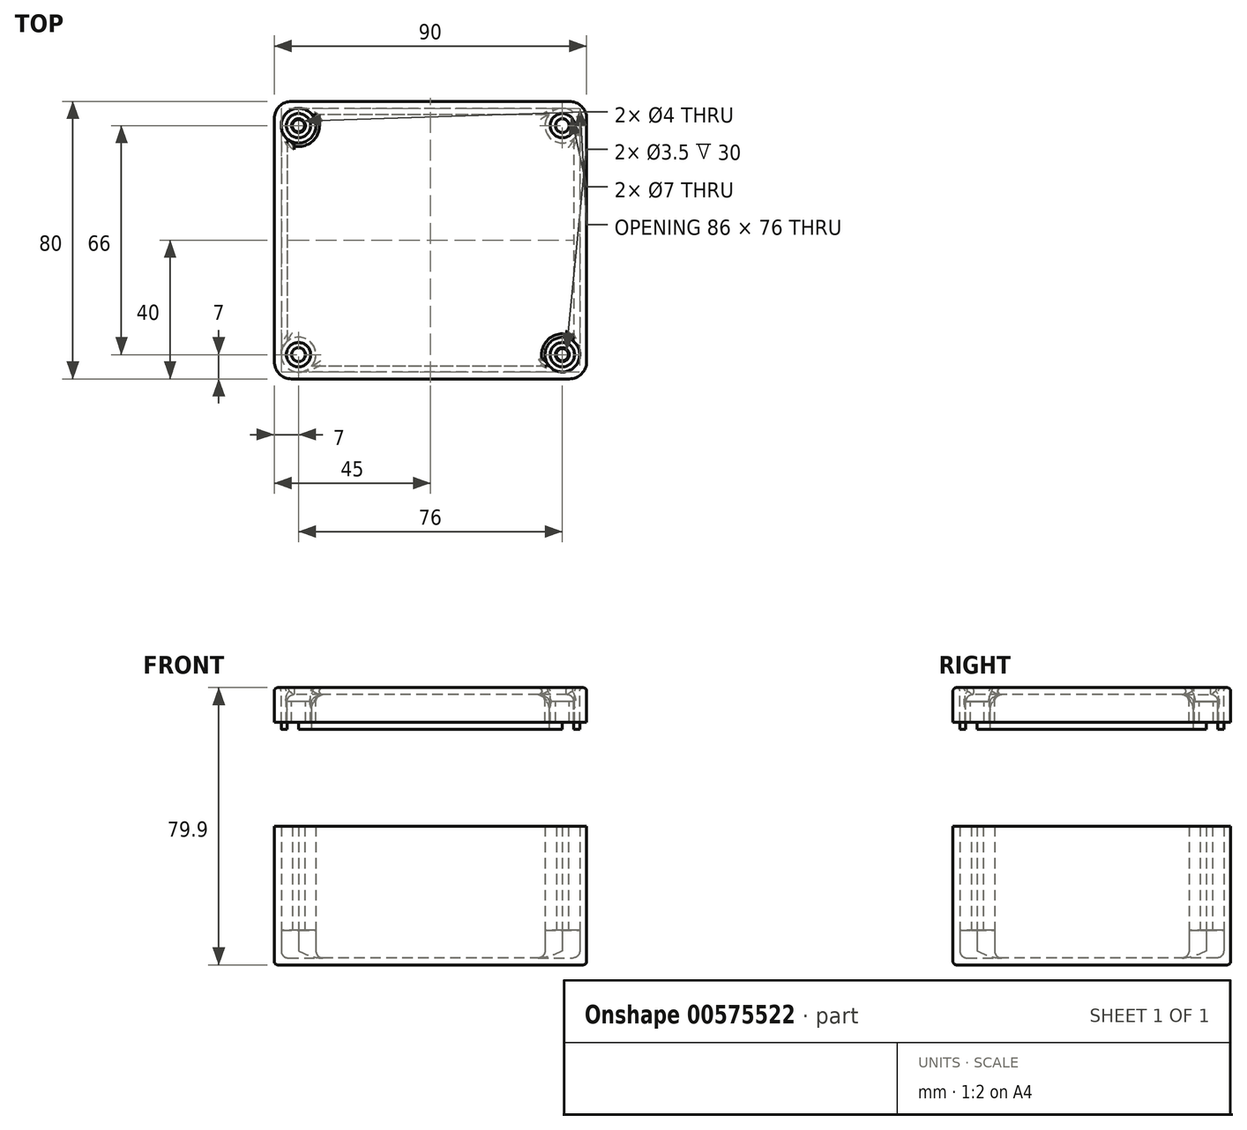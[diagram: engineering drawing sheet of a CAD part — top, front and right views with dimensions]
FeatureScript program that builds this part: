
annotation { "Feature Type Name" : "Feature", "Feature Type Description" : "" }
export const myFeature = defineFeature(function(context is Context, id is Id, definition is map)
    precondition{}
    {
        {
            var Q0;
            Q0=qCreatedBy(makeId("Top.planeOp"),FACE);
            var sketch = newSketch(context, id + "F0", { "sketchPlane" : qUnion([Q0])});
            skLineSegment(sketch, "E0.bottom", {"start": v(40, 40) * mm, "end": v(-40, 40) * mm});
            skLineSegment(sketch, "E0.top", {"start": v(40, -40) * mm, "end": v(-40, -40) * mm});
            skLineSegment(sketch, "E0.left", {"start": v(45, 35) * mm, "end": v(45, -35) * mm});
            skLineSegment(sketch, "E0.right", {"start": v(-45, 35) * mm, "end": v(-45, -35) * mm});
            skPoint(sketch, "E0.middle", {"position": v(0, 0) * mm});
            skPoint(sketch, "E1.visualSharp", {"position": v(-45, 40) * mm});
            skArc(sketch, "E1.filletArc", {"start": v(-40, 40) * mm, "mid": v(-43.54, 38.54) * mm, "end": v(-45, 35) * mm});
            skPoint(sketch, "E2.visualSharp", {"position": v(45, 40) * mm});
            skArc(sketch, "E2.filletArc", {"start": v(45, 35) * mm, "mid": v(43.54, 38.54) * mm, "end": v(40, 40) * mm});
            skPoint(sketch, "E3.visualSharp", {"position": v(-45, -40) * mm});
            skArc(sketch, "E3.filletArc", {"start": v(-45, -35) * mm, "mid": v(-43.54, -38.54) * mm, "end": v(-40, -40) * mm});
            skPoint(sketch, "E4.visualSharp", {"position": v(45, -40) * mm});
            skArc(sketch, "E4.filletArc", {"start": v(40, -40) * mm, "mid": v(43.54, -38.54) * mm, "end": v(45, -35) * mm});
            skLineSegment(sketch, "E5.0", {"start": v(38, -38) * mm, "end": v(-38, -38) * mm});
            skLineSegment(sketch, "E5.1", {"start": v(43, 33) * mm, "end": v(43, -33) * mm});
            skLineSegment(sketch, "E5.2", {"start": v(38, 38) * mm, "end": v(-38, 38) * mm});
            skLineSegment(sketch, "E5.3", {"start": v(-43, 33) * mm, "end": v(-43, -33) * mm});
            skPoint(sketch, "E6.visualSharp", {"position": v(43, 38) * mm});
            skArc(sketch, "E6.filletArc", {"start": v(43, 33) * mm, "mid": v(41.54, 36.54) * mm, "end": v(38, 38) * mm});
            skPoint(sketch, "E7.visualSharp", {"position": v(43, -38) * mm});
            skArc(sketch, "E7.filletArc", {"start": v(38, -38) * mm, "mid": v(41.54, -36.54) * mm, "end": v(43, -33) * mm});
            skPoint(sketch, "E8.visualSharp", {"position": v(-43, -38) * mm});
            skArc(sketch, "E8.filletArc", {"start": v(-43, -33) * mm, "mid": v(-41.54, -36.54) * mm, "end": v(-38, -38) * mm});
            skPoint(sketch, "E9.visualSharp", {"position": v(-43, 38) * mm});
            skArc(sketch, "E9.filletArc", {"start": v(-38, 38) * mm, "mid": v(-41.54, 36.54) * mm, "end": v(-43, 33) * mm});
            skLineSegment(sketch, "E10", {"start": v(0, 38) * mm, "end": v(0, -38) * mm, "construction": true});
            skCircle(sketch, "E11", {"center": v(-38, 33) * mm, "radius": 5 * mm});
            skCircle(sketch, "E12", {"center": v(-38, 33) * mm, "radius": 1.75 * mm});
            skLineSegment(sketch, "E13", {"start": v(-43, 0) * mm, "end": v(43, 0) * mm, "construction": true});
            skCircle(sketch, "E14.MirrorC", {"center": v(-38, -33) * mm, "radius": 5 * mm});
            skCircle(sketch, "E15.MirrorC", {"center": v(-38, -33) * mm, "radius": 1.75 * mm});
            skCircle(sketch, "E16.MirrorC", {"center": v(38, 33) * mm, "radius": 5 * mm});
            skCircle(sketch, "E17.MirrorC", {"center": v(38, 33) * mm, "radius": 1.75 * mm});
            skCircle(sketch, "E18.MirrorC", {"center": v(38, -33) * mm, "radius": 5 * mm});
            skCircle(sketch, "E19.MirrorC", {"center": v(38, -33) * mm, "radius": 1.75 * mm});
            skSolve(sketch);
        }
        {
            var Q0;
            {var subQ2=sQuery(id+"F0.wireOp",EDGE,"E5.0");Q0=makeQuery(id+"F0.imprint","IMPRINT",FACE,{"disambiguationData":[TD([[makeQuery(id+"F0.imprint","IMPRINT",EDGE,{"derivedFrom":subQ2}),-1.0]])]});}
            extrude(context, id + "F1", {"entities" : qUnion([Q0]), "depth" : 2 * mm, "offsetDistance" : 25 * mm});
        }
        {
            var Q0;
            Q0=makeQuery(id+"F0.imprint","IMPRINT",FACE,{"disambiguationData":[TD([[makeQuery(id+"F0.imprint","IMPRINT",EDGE,{"derivedFrom":sQuery(id+"F0.wireOp",EDGE,"E12")}),-1.0]])]});
            var Q1;
            Q1=makeQuery(id+"F0.imprint","IMPRINT",FACE,{"disambiguationData":[TD([[makeQuery(id+"F0.imprint","IMPRINT",EDGE,{"derivedFrom":sQuery(id+"F0.wireOp",EDGE,"E15.MirrorC")}),1.0]])]});
            var Q2;
            Q2=makeQuery(id+"F0.imprint","IMPRINT",FACE,{"disambiguationData":[TD([[makeQuery(id+"F0.imprint","IMPRINT",EDGE,{"derivedFrom":sQuery(id+"F0.wireOp",EDGE,"E0.bottom")}),1.0]])]});
            var Q3;
            Q3=makeQuery(id+"F0.imprint","IMPRINT",FACE,{"disambiguationData":[TD([[makeQuery(id+"F0.imprint","IMPRINT",EDGE,{"derivedFrom":sQuery(id+"F0.wireOp",EDGE,"E19.MirrorC")}),-1.0]])]});
            var Q4;
            Q4=makeQuery(id+"F0.imprint","IMPRINT",FACE,{"disambiguationData":[TD([[makeQuery(id+"F0.imprint","IMPRINT",EDGE,{"derivedFrom":sQuery(id+"F0.wireOp",EDGE,"E17.MirrorC")}),1.0]])]});
            extrude(context, id + "F2", {"entities" : qUnion([Q0, Q1, Q2, Q3, Q4]), "operationType" : NewBodyOperationType.ADD, "depth" : 40 * mm, "offsetDistance" : 25 * mm});
        }
        {
            var Q0;
            Q0=makeQuery(id+"F0.imprint","IMPRINT",FACE,{"disambiguationData":[TD([[makeQuery(id+"F0.imprint","IMPRINT",EDGE,{"derivedFrom":sQuery(id+"F0.wireOp",EDGE,"E17.MirrorC")}),-1.0]])]});
            var Q1;
            Q1=makeQuery(id+"F0.imprint","IMPRINT",FACE,{"disambiguationData":[TD([[makeQuery(id+"F0.imprint","IMPRINT",EDGE,{"derivedFrom":sQuery(id+"F0.wireOp",EDGE,"E19.MirrorC")}),1.0]])]});
            var Q2;
            Q2=makeQuery(id+"F0.imprint","IMPRINT",FACE,{"disambiguationData":[TD([[makeQuery(id+"F0.imprint","IMPRINT",EDGE,{"derivedFrom":sQuery(id+"F0.wireOp",EDGE,"E15.MirrorC")}),-1.0]])]});
            var Q3;
            Q3=makeQuery(id+"F0.imprint","IMPRINT",FACE,{"disambiguationData":[TD([[makeQuery(id+"F0.imprint","IMPRINT",EDGE,{"derivedFrom":sQuery(id+"F0.wireOp",EDGE,"E12")}),1.0]])]});
            extrude(context, id + "F3", {"entities" : qUnion([Q0, Q1, Q2, Q3]), "operationType" : NewBodyOperationType.ADD, "depth" : 10 * mm, "offsetDistance" : 25 * mm});
        }
        {
            var Q0;
            Q0=qCreatedBy(makeId("Top.planeOp"),FACE);
            cPlane(context, id + "F4", {"entities" : qUnion([Q0]), "cplaneType" : CPlaneType.OFFSET, "offset" : 79.9 * mm, "width" : 150 * mm, "height" : 150 * mm});
        }
        {
            var Q0;
            Q0=qCreatedBy(id+"F4.planeOp",FACE);
            var sketch = newSketch(context, id + "F5", { "sketchPlane" : qUnion([Q0])});
            skLineSegment(sketch, "E20.bottom", {"start": v(-40, 40) * mm, "end": v(40, 40) * mm});
            skLineSegment(sketch, "E20.top", {"start": v(-40, -40) * mm, "end": v(40, -40) * mm});
            skLineSegment(sketch, "E20.left", {"start": v(-45, 35) * mm, "end": v(-45, -35) * mm});
            skLineSegment(sketch, "E20.right", {"start": v(45, 35) * mm, "end": v(45, -35) * mm});
            skPoint(sketch, "E20.middle", {"position": v(0, 0) * mm});
            skPoint(sketch, "E21.visualSharp", {"position": v(-45, 40) * mm});
            skArc(sketch, "E21.filletArc", {"start": v(-40, 40) * mm, "mid": v(-43.54, 38.54) * mm, "end": v(-45, 35) * mm});
            skPoint(sketch, "E22.visualSharp", {"position": v(-45, -40) * mm});
            skArc(sketch, "E22.filletArc", {"start": v(-45, -35) * mm, "mid": v(-43.54, -38.54) * mm, "end": v(-40, -40) * mm});
            skPoint(sketch, "E23.visualSharp", {"position": v(45, -40) * mm});
            skArc(sketch, "E23.filletArc", {"start": v(40, -40) * mm, "mid": v(43.54, -38.54) * mm, "end": v(45, -35) * mm});
            skPoint(sketch, "E24.visualSharp", {"position": v(45, 40) * mm});
            skArc(sketch, "E24.filletArc", {"start": v(45, 35) * mm, "mid": v(43.54, 38.54) * mm, "end": v(40, 40) * mm});
            skLineSegment(sketch, "E25.0", {"start": v(-38, 38) * mm, "end": v(38, 38) * mm});
            skLineSegment(sketch, "E25.1", {"start": v(-43, 33) * mm, "end": v(-43, -33) * mm});
            skLineSegment(sketch, "E25.2", {"start": v(-38, -38) * mm, "end": v(38, -38) * mm});
            skLineSegment(sketch, "E25.3", {"start": v(43, 33) * mm, "end": v(43, -33) * mm});
            skPoint(sketch, "E26.visualSharp", {"position": v(-43, 38) * mm});
            skArc(sketch, "E26.filletArc", {"start": v(-38, 38) * mm, "mid": v(-41.54, 36.54) * mm, "end": v(-43, 33) * mm});
            skPoint(sketch, "E27.visualSharp", {"position": v(-43, -38) * mm});
            skArc(sketch, "E27.filletArc", {"start": v(-43, -33) * mm, "mid": v(-41.54, -36.54) * mm, "end": v(-38, -38) * mm});
            skPoint(sketch, "E28.visualSharp", {"position": v(43, -38) * mm});
            skArc(sketch, "E28.filletArc", {"start": v(38, -38) * mm, "mid": v(41.54, -36.54) * mm, "end": v(43, -33) * mm});
            skPoint(sketch, "E29.visualSharp", {"position": v(43, 38) * mm});
            skArc(sketch, "E29.filletArc", {"start": v(43, 33) * mm, "mid": v(41.54, 36.54) * mm, "end": v(38, 38) * mm});
            skCircle(sketch, "E30", {"center": v(-38, 33) * mm, "radius": 5 * mm});
            skCircle(sketch, "E31", {"center": v(-38, 33) * mm, "radius": 2 * mm});
            skLineSegment(sketch, "E32", {"start": v(0, 38) * mm, "end": v(0, -38) * mm, "construction": true});
            skLineSegment(sketch, "E33", {"start": v(-43, 0) * mm, "end": v(43, 0) * mm, "construction": true});
            skCircle(sketch, "E34.MirrorC", {"center": v(38, 33) * mm, "radius": 2 * mm});
            skCircle(sketch, "E35.MirrorC", {"center": v(38, 33) * mm, "radius": 5 * mm});
            skCircle(sketch, "E36.MirrorC", {"center": v(-38, -33) * mm, "radius": 5 * mm});
            skCircle(sketch, "E37.MirrorC", {"center": v(-38, -33) * mm, "radius": 2 * mm});
            skCircle(sketch, "E38.MirrorC", {"center": v(38, -33) * mm, "radius": 2 * mm});
            skCircle(sketch, "E39.MirrorC", {"center": v(38, -33) * mm, "radius": 5 * mm});
            skLineSegment(sketch, "E40", {"start": v(-41.3, 29.24) * mm, "end": v(-41.3, -29.24) * mm});
            skLineSegment(sketch, "E41", {"start": v(-34.24, 36.3) * mm, "end": v(34.24, 36.3) * mm});
            skLineSegment(sketch, "E42", {"start": v(41.3, 29.24) * mm, "end": v(41.3, -29.24) * mm});
            skLineSegment(sketch, "E43", {"start": v(34.24, -36.3) * mm, "end": v(-34.24, -36.3) * mm});
            skCircle(sketch, "E44", {"center": v(-38, -33) * mm, "radius": 3.5 * mm});
            skCircle(sketch, "E45.MirrorC", {"center": v(38, -33) * mm, "radius": 3.5 * mm});
            skCircle(sketch, "E46.MirrorC", {"center": v(-38, 33) * mm, "radius": 3.5 * mm});
            skCircle(sketch, "E47.MirrorC", {"center": v(38, 33) * mm, "radius": 3.5 * mm});
            skSolve(sketch);
        }
        {
            var Q0;
            Q0=makeQuery(id+"F5.imprint","IMPRINT",FACE,{"disambiguationData":[TD([[makeQuery(id+"F5.imprint","IMPRINT",EDGE,{"derivedFrom":sQuery(id+"F5.wireOp",EDGE,"E46.MirrorC")}),1.0]])]});
            var Q1;
            Q1=makeQuery(id+"F5.imprint","IMPRINT",FACE,{"disambiguationData":[TD([[makeQuery(id+"F5.imprint","IMPRINT",EDGE,{"derivedFrom":sQuery(id+"F5.wireOp",EDGE,"E20.bottom")}),-1.0]])]});
            var Q2;
            Q2=makeQuery(id+"F5.imprint","IMPRINT",FACE,{"disambiguationData":[TD([[makeQuery(id+"F5.imprint","IMPRINT",EDGE,{"derivedFrom":sQuery(id+"F5.wireOp",EDGE,"E44")}),-1.0]])]});
            var Q3;
            Q3=makeQuery(id+"F5.imprint","IMPRINT",FACE,{"disambiguationData":[TD([[makeQuery(id+"F5.imprint","IMPRINT",EDGE,{"derivedFrom":sQuery(id+"F5.wireOp",EDGE,"E45.MirrorC")}),1.0]])]});
            var Q4;
            Q4=makeQuery(id+"F5.imprint","IMPRINT",FACE,{"disambiguationData":[TD([[makeQuery(id+"F5.imprint","IMPRINT",EDGE,{"derivedFrom":sQuery(id+"F5.wireOp",EDGE,"E47.MirrorC")}),-1.0]])]});
            extrude(context, id + "F6", {"entities" : qUnion([Q0, Q1, Q2, Q3, Q4]), "depth" : -10 * mm, "offsetDistance" : 25 * mm});
        }
        {
            var Q0;
            Q0=makeQuery(id+"F5.imprint","IMPRINT",FACE,{"disambiguationData":[TD([[makeQuery(id+"F5.imprint","IMPRINT",EDGE,{"derivedFrom":sQuery(id+"F5.wireOp",EDGE,"E31")}),-1.0]])]});
            var Q1;
            Q1=makeQuery(id+"F5.imprint","IMPRINT",FACE,{"disambiguationData":[TD([[makeQuery(id+"F5.imprint","IMPRINT",EDGE,{"derivedFrom":sQuery(id+"F5.wireOp",EDGE,"E37.MirrorC")}),1.0]])]});
            var Q2;
            Q2=makeQuery(id+"F5.imprint","IMPRINT",FACE,{"disambiguationData":[TD([[makeQuery(id+"F5.imprint","IMPRINT",EDGE,{"derivedFrom":sQuery(id+"F5.wireOp",EDGE,"E38.MirrorC")}),-1.0]])]});
            var Q3;
            Q3=makeQuery(id+"F5.imprint","IMPRINT",FACE,{"disambiguationData":[TD([[makeQuery(id+"F5.imprint","IMPRINT",EDGE,{"derivedFrom":sQuery(id+"F5.wireOp",EDGE,"E34.MirrorC")}),1.0]])]});
            extrude(context, id + "F7", {"entities" : qUnion([Q0, Q1, Q2, Q3]), "operationType" : NewBodyOperationType.ADD, "depth" : -10 * mm, "offsetDistance" : 25 * mm});
        }
        {
            var Q0;
            Q0=makeQuery(id+"F5.imprint","IMPRINT",FACE,{"disambiguationData":[TD([[makeQuery(id+"F5.imprint","IMPRINT",EDGE,{"derivedFrom":sQuery(id+"F5.wireOp",EDGE,"E31")}),-1.0]])]});
            var Q1;
            Q1=makeQuery(id+"F5.imprint","IMPRINT",FACE,{"disambiguationData":[TD([[makeQuery(id+"F5.imprint","IMPRINT",EDGE,{"derivedFrom":sQuery(id+"F5.wireOp",EDGE,"E37.MirrorC")}),1.0]])]});
            var Q2;
            Q2=makeQuery(id+"F5.imprint","IMPRINT",FACE,{"disambiguationData":[TD([[makeQuery(id+"F5.imprint","IMPRINT",EDGE,{"derivedFrom":sQuery(id+"F5.wireOp",EDGE,"E38.MirrorC")}),-1.0]])]});
            var Q3;
            Q3=makeQuery(id+"F5.imprint","IMPRINT",FACE,{"disambiguationData":[TD([[makeQuery(id+"F5.imprint","IMPRINT",EDGE,{"derivedFrom":sQuery(id+"F5.wireOp",EDGE,"E34.MirrorC")}),1.0]])]});
            extrude(context, id + "F8", {"entities" : qUnion([Q0, Q1, Q2, Q3]), "operationType" : NewBodyOperationType.REMOVE, "oppositeDirection" : true, "depth" : 4 * mm, "offsetDistance" : 25 * mm});
        }
        {
            var Q0;
            {var subQ0=sQuery(id+"F5.wireOp",EDGE,"E25.0");Q0=makeQuery(id+"F5.imprint","IMPRINT",FACE,{"disambiguationData":[TD([[makeQuery(id+"F5.imprint","IMPRINT",EDGE,{"derivedFrom":subQ0}),-1.0]])]});}
            var Q1;
            {var subQ0=sQuery(id+"F5.wireOp",EDGE,"E25.1");Q1=makeQuery(id+"F5.imprint","IMPRINT",FACE,{"disambiguationData":[TD([[makeQuery(id+"F5.imprint","IMPRINT",EDGE,{"derivedFrom":subQ0}),1.0]])]});}
            var Q2;
            {var subQ0=sQuery(id+"F5.wireOp",EDGE,"E25.2");Q2=makeQuery(id+"F5.imprint","IMPRINT",FACE,{"disambiguationData":[TD([[makeQuery(id+"F5.imprint","IMPRINT",EDGE,{"derivedFrom":subQ0}),1.0]])]});}
            var Q3;
            {var subQ0=sQuery(id+"F5.wireOp",EDGE,"E25.3");Q3=makeQuery(id+"F5.imprint","IMPRINT",FACE,{"disambiguationData":[TD([[makeQuery(id+"F5.imprint","IMPRINT",EDGE,{"derivedFrom":subQ0}),-1.0]])]});}
            extrude(context, id + "F9", {"entities" : qUnion([Q0, Q1, Q2, Q3]), "operationType" : NewBodyOperationType.ADD, "depth" : -12 * mm, "offsetDistance" : 25 * mm});
        }
        {
            var Q0;
            {var subQ5=sQuery(id+"F5.wireOp",EDGE,"E40");Q0=makeQuery(id+"F5.imprint","IMPRINT",FACE,{"disambiguationData":[TD([[makeQuery(id+"F5.imprint","IMPRINT",EDGE,{"derivedFrom":subQ5}),1.0]])]});}
            extrude(context, id + "F10", {"entities" : qUnion([Q0]), "operationType" : NewBodyOperationType.ADD, "depth" : -2 * mm, "offsetDistance" : 25 * mm});
        }
        {
            var Q0;
            Q0=makeQuery(id+"F1.opExtrude","CAP_FACE",FACE,{"disambiguationData":[OSD([sQuery(id+"F0.wireOp",EDGE,"E5.0"),sQuery(id+"F0.wireOp",EDGE,"E5.1"),sQuery(id+"F0.wireOp",EDGE,"E5.2"),sQuery(id+"F0.wireOp",EDGE,"E5.3"),sQuery(id+"F0.wireOp",EDGE,"E11"),sQuery(id+"F0.wireOp",EDGE,"E14.MirrorC"),sQuery(id+"F0.wireOp",EDGE,"E16.MirrorC"),sQuery(id+"F0.wireOp",EDGE,"E18.MirrorC")])],"isStart":false});
            fillet(context, id + "F11", {"entities" : qUnion([Q0]), "radius" : 2 * mm, "tangentPropagation" : true, "allowEdgeOverflow" : false});
        }
        {
            var Q0;
            {var subQ0=sQuery(id+"F0.wireOp",EDGE,"E19.MirrorC");var subQ1=sQuery(id+"F0.wireOp",EDGE,"E17.MirrorC");var subQ2=sQuery(id+"F0.wireOp",EDGE,"E15.MirrorC");var subQ3=sQuery(id+"F0.wireOp",EDGE,"E12");var subQ4=sQuery(id+"F0.wireOp",EDGE,"E18.MirrorC");var subQ5=sQuery(id+"F0.wireOp",EDGE,"E16.MirrorC");var subQ6=sQuery(id+"F0.wireOp",EDGE,"E14.MirrorC");var subQ7=sQuery(id+"F0.wireOp",EDGE,"E11");var subQ8=sQuery(id+"F0.wireOp",EDGE,"E5.3");var subQ9=sQuery(id+"F0.wireOp",EDGE,"E5.2");var subQ10=sQuery(id+"F0.wireOp",EDGE,"E5.1");var subQ11=sQuery(id+"F0.wireOp",EDGE,"E5.0");Q0=makeQuery(id+"F3.boolean.opBoolean","MERGE",FACE,{"derivedFrom":[makeQuery(id+"F2.boolean.opBoolean","MERGE",FACE,{"derivedFrom":[makeQuery(id+"F1.opExtrude","CAP_FACE",FACE,{"disambiguationData":[OSD([subQ11,subQ10,subQ9,subQ8,subQ7,subQ6,subQ5,subQ4])],"isStart":true}),makeQuery(id+"F2.opExtrude","CAP_FACE",FACE,{"disambiguationData":[OSD([sQuery(id+"F0.wireOp",EDGE,"E0.bottom"),sQuery(id+"F0.wireOp",EDGE,"E0.top"),sQuery(id+"F0.wireOp",EDGE,"E0.left"),sQuery(id+"F0.wireOp",EDGE,"E0.right"),sQuery(id+"F0.wireOp",EDGE,"E1.filletArc"),sQuery(id+"F0.wireOp",EDGE,"E2.filletArc"),sQuery(id+"F0.wireOp",EDGE,"E3.filletArc"),sQuery(id+"F0.wireOp",EDGE,"E4.filletArc"),subQ11,subQ10,subQ9,subQ8,subQ7,subQ3,subQ6,subQ2,subQ5,subQ1,subQ4,subQ0])],"isStart":true})]}),makeQuery(id+"F3.opExtrude","CAP_FACE",FACE,{"disambiguationData":[OSD([subQ3])],"isStart":true}),makeQuery(id+"F3.opExtrude","CAP_FACE",FACE,{"disambiguationData":[OSD([subQ2])],"isStart":true}),makeQuery(id+"F3.opExtrude","CAP_FACE",FACE,{"disambiguationData":[OSD([subQ1])],"isStart":true}),makeQuery(id+"F3.opExtrude","CAP_FACE",FACE,{"disambiguationData":[OSD([subQ0])],"isStart":true})]});}
            fillet(context, id + "F12", {"entities" : qUnion([Q0]), "radius" : 1 * mm, "tangentPropagation" : true, "allowEdgeOverflow" : false});
        }
        {
            var Q0;
            Q0=makeQuery(id+"F10.opExtrude","CAP_FACE",FACE,{"disambiguationData":[OSD([sQuery(id+"F5.wireOp",EDGE,"E30"),sQuery(id+"F5.wireOp",EDGE,"E35.MirrorC"),sQuery(id+"F5.wireOp",EDGE,"E36.MirrorC"),sQuery(id+"F5.wireOp",EDGE,"E39.MirrorC"),sQuery(id+"F5.wireOp",EDGE,"E40"),sQuery(id+"F5.wireOp",EDGE,"E41"),sQuery(id+"F5.wireOp",EDGE,"E42"),sQuery(id+"F5.wireOp",EDGE,"E43")])],"isStart":false});
            fillet(context, id + "F13", {"entities" : qUnion([Q0]), "radius" : 2 * mm, "tangentPropagation" : true, "allowEdgeOverflow" : false});
        }
        {
            var Q0;
            {var subQ0=sQuery(id+"F5.wireOp",EDGE,"E43");var subQ1=sQuery(id+"F5.wireOp",EDGE,"E42");var subQ2=sQuery(id+"F5.wireOp",EDGE,"E41");var subQ3=sQuery(id+"F5.wireOp",EDGE,"E40");var subQ4=sQuery(id+"F5.wireOp",EDGE,"E39.MirrorC");var subQ5=sQuery(id+"F5.wireOp",EDGE,"E36.MirrorC");var subQ6=sQuery(id+"F5.wireOp",EDGE,"E35.MirrorC");var subQ7=sQuery(id+"F5.wireOp",EDGE,"E30");var subQ8=sQuery(id+"F5.wireOp",EDGE,"E25.3");var subQ9=sQuery(id+"F5.wireOp",EDGE,"E25.2");var subQ10=sQuery(id+"F5.wireOp",EDGE,"E25.1");var subQ11=sQuery(id+"F5.wireOp",EDGE,"E25.0");var subQ12=sQuery(id+"F5.wireOp",EDGE,"E45.MirrorC");var subQ13=sQuery(id+"F5.wireOp",EDGE,"E44");var subQ14=sQuery(id+"F5.wireOp",EDGE,"E47.MirrorC");var subQ15=sQuery(id+"F5.wireOp",EDGE,"E46.MirrorC");Q0=makeQuery(id+"F10.boolean.opBoolean","MERGE",FACE,{"derivedFrom":[makeQuery(id+"F9.boolean.opBoolean","MERGE",FACE,{"derivedFrom":[makeQuery(id+"F7.boolean.opBoolean","MERGE",FACE,{"derivedFrom":[makeQuery(id+"F6.opExtrude","CAP_FACE",FACE,{"disambiguationData":[OSD([sQuery(id+"F5.wireOp",EDGE,"E20.bottom"),sQuery(id+"F5.wireOp",EDGE,"E20.top"),sQuery(id+"F5.wireOp",EDGE,"E20.left"),sQuery(id+"F5.wireOp",EDGE,"E20.right"),sQuery(id+"F5.wireOp",EDGE,"E21.filletArc"),sQuery(id+"F5.wireOp",EDGE,"E22.filletArc"),sQuery(id+"F5.wireOp",EDGE,"E23.filletArc"),sQuery(id+"F5.wireOp",EDGE,"E24.filletArc"),subQ11,subQ10,subQ9,subQ8,subQ7,subQ6,subQ5,subQ4,subQ13,subQ12,subQ15,subQ14])],"isStart":true}),makeQuery(id+"F7.opExtrude","CAP_FACE",FACE,{"disambiguationData":[OSD([sQuery(id+"F5.wireOp",EDGE,"E31"),subQ15])],"isStart":true}),makeQuery(id+"F7.opExtrude","CAP_FACE",FACE,{"disambiguationData":[OSD([sQuery(id+"F5.wireOp",EDGE,"E34.MirrorC"),subQ14])],"isStart":true}),makeQuery(id+"F7.opExtrude","CAP_FACE",FACE,{"disambiguationData":[OSD([sQuery(id+"F5.wireOp",EDGE,"E37.MirrorC"),subQ13])],"isStart":true}),makeQuery(id+"F7.opExtrude","CAP_FACE",FACE,{"disambiguationData":[OSD([sQuery(id+"F5.wireOp",EDGE,"E38.MirrorC"),subQ12])],"isStart":true})]}),makeQuery(id+"F9.opExtrude","CAP_FACE",FACE,{"disambiguationData":[OSD([subQ11,subQ7,subQ6,subQ2])],"isStart":true}),makeQuery(id+"F9.opExtrude","CAP_FACE",FACE,{"disambiguationData":[OSD([subQ10,subQ7,subQ5,subQ3])],"isStart":true}),makeQuery(id+"F9.opExtrude","CAP_FACE",FACE,{"disambiguationData":[OSD([subQ9,subQ5,subQ4,subQ0])],"isStart":true}),makeQuery(id+"F9.opExtrude","CAP_FACE",FACE,{"disambiguationData":[OSD([subQ8,subQ6,subQ4,subQ1])],"isStart":true})]}),makeQuery(id+"F10.opExtrude","CAP_FACE",FACE,{"disambiguationData":[OSD([subQ7,subQ6,subQ5,subQ4,subQ3,subQ2,subQ1,subQ0])],"isStart":true})]});}
            fillet(context, id + "F14", {"entities" : qUnion([Q0]), "radius" : 1 * mm, "tangentPropagation" : true, "allowEdgeOverflow" : false});
        }
    });
